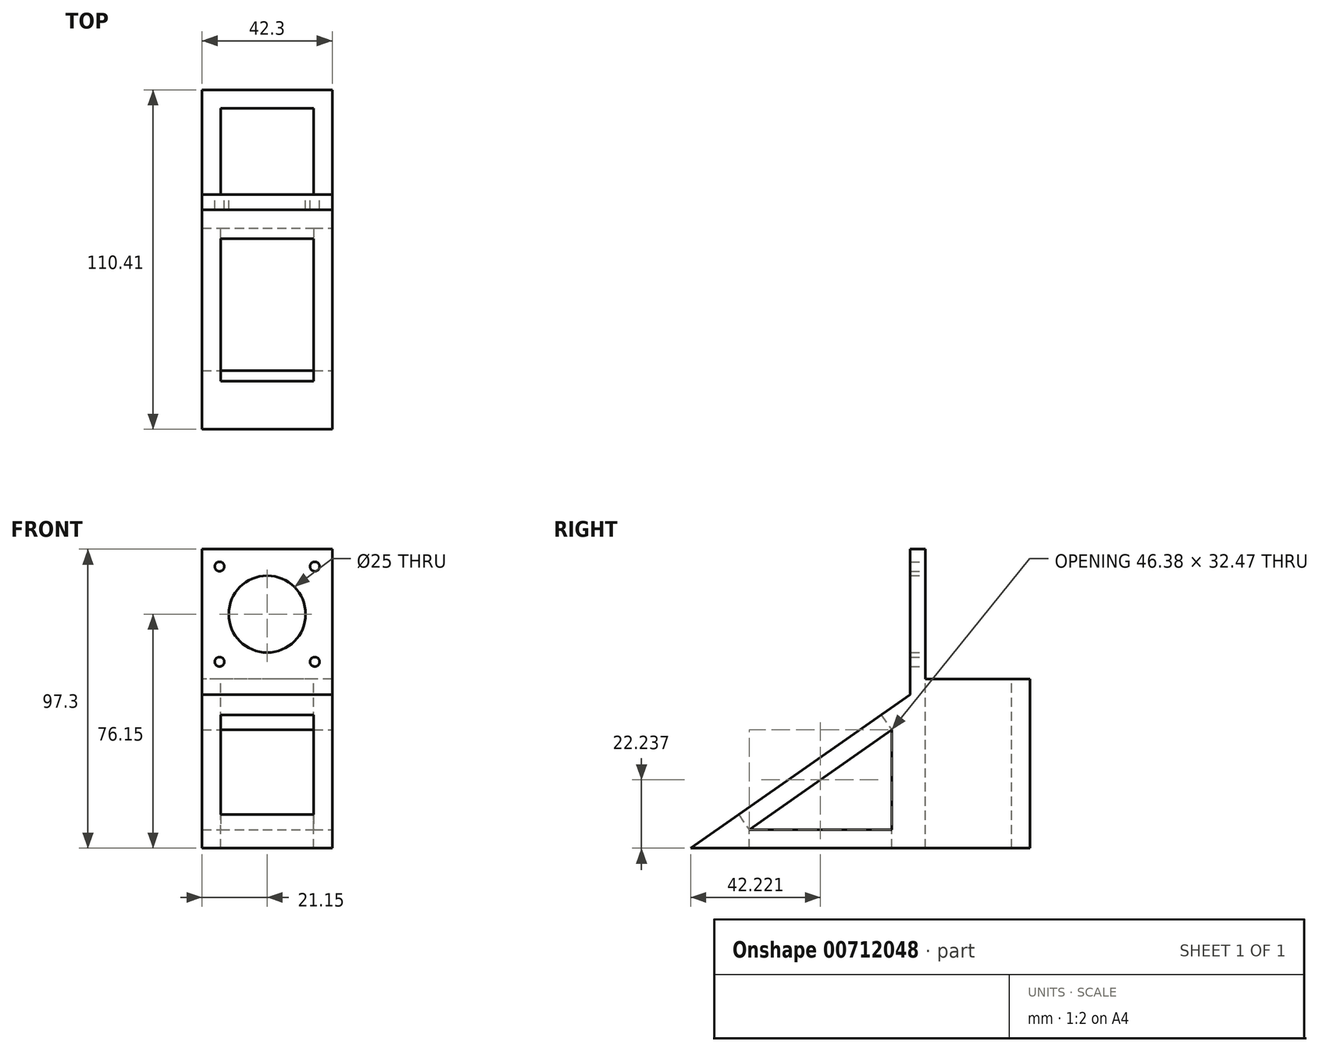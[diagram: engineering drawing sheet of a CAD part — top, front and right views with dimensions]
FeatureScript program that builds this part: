
annotation { "Feature Type Name" : "Feature", "Feature Type Description" : "" }
export const myFeature = defineFeature(function(context is Context, id is Id, definition is map)
    precondition{}
    {
        {
            var Q0;
            Q0=qCreatedBy(makeId("Front.planeOp"),FACE);
            var sketch = newSketch(context, id + "F0", { "sketchPlane" : qUnion([Q0])});
            skLineSegment(sketch, "E0.bottom", {"start": v(21.15, -21.15) * mm, "end": v(-21.15, -21.15) * mm});
            skLineSegment(sketch, "E0.top", {"start": v(21.15, 21.15) * mm, "end": v(-21.15, 21.15) * mm});
            skLineSegment(sketch, "E0.left", {"start": v(21.15, -21.15) * mm, "end": v(21.15, 21.15) * mm});
            skLineSegment(sketch, "E0.right", {"start": v(-21.15, -21.15) * mm, "end": v(-21.15, 21.15) * mm});
            skPoint(sketch, "E0.middle", {"position": v(0, 0) * mm});
            skPoint(sketch, "E1", {"position": v(15.5, 15.5) * mm});
            skPoint(sketch, "E2", {"position": v(-15.5, 15.5) * mm});
            skPoint(sketch, "E3", {"position": v(-15.5, -15.5) * mm});
            skPoint(sketch, "E4", {"position": v(15.5, -15.5) * mm});
            skCircle(sketch, "E5", {"center": v(0, 0) * mm, "radius": 12.5 * mm});
            skLineSegment(sketch, "E6", {"start": v(-21.15, -21.15) * mm, "end": v(-21.15, -26.15) * mm});
            skLineSegment(sketch, "E7", {"start": v(-21.15, -26.15) * mm, "end": v(21.15, -26.15) * mm});
            skLineSegment(sketch, "E8", {"start": v(21.15, -26.15) * mm, "end": v(21.15, -21.15) * mm});
            skSolve(sketch);
        }
        {
            var Q0;
            Q0=makeQuery(id+"F0.imprint","IMPRINT",FACE,{"disambiguationData":[TD([[makeQuery(id+"F0.imprint","IMPRINT",EDGE,{"derivedFrom":sQuery(id+"F0.wireOp",EDGE,"E0.bottom")}),-1.0]])]});
            var Q1;
            Q1=makeQuery(id+"F0.imprint","IMPRINT",FACE,{"disambiguationData":[TD([[makeQuery(id+"F0.imprint","IMPRINT",EDGE,{"derivedFrom":sQuery(id+"F0.wireOp",EDGE,"E0.top")}),1.0]])]});
            extrude(context, id + "F1", {"entities" : qUnion([Q0, Q1]), "depth" : 5 * mm, "offsetDistance" : 25 * mm});
        }
        {
            var Q0;
            Q0=sQuery(id+"F0.wireOp",VERTEX,"E2");
            var Q1;
            Q1=sQuery(id+"F0.wireOp",VERTEX,"E3");
            var Q2;
            Q2=sQuery(id+"F0.wireOp",VERTEX,"E4");
            var Q3;
            Q3=sQuery(id+"F0.wireOp",VERTEX,"E1");
            var Q4;
            Q4=makeQuery(id+"F1.opExtrude","SWEPT_BODY",BODY,{"disambiguationData":[OSD([sQuery(id+"F0.wireOp",EDGE,"E0.bottom"),sQuery(id+"F0.wireOp",EDGE,"E0.top"),sQuery(id+"F0.wireOp",EDGE,"E0.left"),sQuery(id+"F0.wireOp",EDGE,"E0.right")])]});
            hole(context, id + "F2", {"style" : HoleStyle.SIMPLE, "endStyle" : HoleEndStyle.THROUGH, "oppositeDirection" : true, "holeDiameter" : 3.1 * mm, "majorDiameter" : 5 * mm, "isTappedThrough" : true, "tappedDepth" : 12 * mm, "tapClearance" : 3, "locations" : qUnion([Q0, Q1, Q2, Q3]), "scope" : qUnion([Q4])});
        }
        {
            var Q0;
            Q0=makeQuery(id+"F0.imprint","IMPRINT",FACE,{"disambiguationData":[TD([[makeQuery(id+"F0.imprint","IMPRINT",EDGE,{"derivedFrom":sQuery(id+"F0.wireOp",EDGE,"E0.bottom")}),1.0]])]});
            extrude(context, id + "F3", {"entities" : qUnion([Q0]), "operationType" : NewBodyOperationType.ADD, "depth" : 5 * mm, "offsetDistance" : 25 * mm});
        }
        {
            var Q0;
            Q0=makeQuery(id+"F0.imprint","IMPRINT",FACE,{"disambiguationData":[TD([[makeQuery(id+"F0.imprint","IMPRINT",EDGE,{"derivedFrom":sQuery(id+"F0.wireOp",EDGE,"E0.bottom")}),1.0]])]});
            extrude(context, id + "F4", {"entities" : qUnion([Q0]), "operationType" : NewBodyOperationType.ADD, "oppositeDirection" : true, "depth" : 34 * mm, "offsetDistance" : 25 * mm});
        }
        {
            var Q0;
            Q0=makeQuery(id+"F4.opExtrude","SWEPT_FACE",FACE,{"disambiguationData":[OSD([sQuery(id+"F0.wireOp",EDGE,"E0.bottom")])]});
            var sketch = newSketch(context, id + "F5", { "sketchPlane" : qUnion([Q0])});
            skLineSegment(sketch, "E9", {"start": v(-15.15, 28) * mm, "end": v(-15.15, 0) * mm});
            skLineSegment(sketch, "E10", {"start": v(-15.15, 0) * mm, "end": v(15.15, 0) * mm});
            skLineSegment(sketch, "E11", {"start": v(15.15, 0) * mm, "end": v(15.15, 28) * mm});
            skLineSegment(sketch, "E12", {"start": v(15.15, 28) * mm, "end": v(-15.15, 28) * mm});
            skSolve(sketch);
        }
        {
            var Q0;
            Q0=makeQuery(id+"F5.imprint","IMPRINT",FACE,{"disambiguationData":[TD([[makeQuery(id+"F5.imprint","IMPRINT",EDGE,{"derivedFrom":sQuery(id+"F5.wireOp",EDGE,"E9")}),1.0]])]});
            extrude(context, id + "F6", {"entities" : qUnion([Q0]), "operationType" : NewBodyOperationType.REMOVE, "oppositeDirection" : true, "depth" : 5 * mm, "offsetDistance" : 25 * mm});
        }
        {
            var Q0;
            {var subQ0=sQuery(id+"F0.wireOp",EDGE,"E7");Q0=makeQuery(id+"F4.boolean.opBoolean","MERGE",FACE,{"derivedFrom":[makeQuery(id+"F3.opExtrude","SWEPT_FACE",FACE,{"disambiguationData":[OSD([subQ0])]}),makeQuery(id+"F4.opExtrude","SWEPT_FACE",FACE,{"disambiguationData":[OSD([subQ0])]})]});}
            extrude(context, id + "F7", {"entities" : qUnion([Q0]), "operationType" : NewBodyOperationType.ADD, "depth" : 50 * mm, "offsetDistance" : 25 * mm});
        }
        {
            var Q0;
            {var subQ0=sQuery(id+"F0.wireOp",EDGE,"E8");Q0=makeQuery(id+"F7.boolean.opBoolean","MERGE",FACE,{"derivedFrom":[makeQuery(id+"F4.boolean.opBoolean","MERGE",FACE,{"derivedFrom":[makeQuery(id+"F3.boolean.opBoolean","MERGE",FACE,{"derivedFrom":[makeQuery(id+"F1.opExtrude","SWEPT_FACE",FACE,{"disambiguationData":[OSD([sQuery(id+"F0.wireOp",EDGE,"E0.left")])]}),makeQuery(id+"F3.opExtrude","SWEPT_FACE",FACE,{"disambiguationData":[OSD([subQ0])]})]}),makeQuery(id+"F4.opExtrude","SWEPT_FACE",FACE,{"disambiguationData":[OSD([subQ0])]})]}),makeQuery(id+"F7.opExtrude","SWEPT_FACE",FACE,{"disambiguationData":[OSD([sQuery(id+"F0.wireOp",EDGE,"E7"),subQ0])]})]});}
            var sketch = newSketch(context, id + "F8", { "sketchPlane" : qUnion([Q0])});
            skLineSegment(sketch, "E13", {"start": v(-5, -76.15) * mm, "end": v(-76.4, -76.15) * mm});
            skLineSegment(sketch, "E14", {"start": v(-76.4, -76.15) * mm, "end": v(-5, -26.15) * mm});
            skLineSegment(sketch, "E15", {"start": v(-5, -26.15) * mm, "end": v(-5, -76.15) * mm});
            skLineSegment(sketch, "E16", {"start": v(-11, -37.68) * mm, "end": v(-11, -70.15) * mm});
            skLineSegment(sketch, "E17", {"start": v(-11, -70.15) * mm, "end": v(-57.38, -70.15) * mm});
            skLineSegment(sketch, "E18", {"start": v(-57.38, -70.15) * mm, "end": v(-11, -37.68) * mm});
            skSolve(sketch);
        }
        {
            var Q0;
            Q0=makeQuery(id+"F8.imprint","IMPRINT",FACE,{"disambiguationData":[TD([[makeQuery(id+"F8.imprint","IMPRINT",EDGE,{"derivedFrom":sQuery(id+"F8.wireOp",EDGE,"E13")}),-1.0]])]});
            extrude(context, id + "F9", {"entities" : qUnion([Q0]), "operationType" : NewBodyOperationType.ADD, "oppositeDirection" : true, "depth" : 42.3 * mm, "offsetDistance" : 25 * mm});
        }
        {
            var Q0;
            Q0=makeQuery(id+"F9.opExtrude","SWEPT_FACE",FACE,{"disambiguationData":[OSD([sQuery(id+"F8.wireOp",EDGE,"E18")])]});
            var sketch = newSketch(context, id + "F10", { "sketchPlane" : qUnion([Q0])});
            skLineSegment(sketch, "E19", {"start": v(15.15, 30.62) * mm, "end": v(-15.15, 30.62) * mm});
            skLineSegment(sketch, "E20", {"start": v(-15.15, 30.62) * mm, "end": v(-15.15, 87.24) * mm});
            skLineSegment(sketch, "E21", {"start": v(-15.15, 87.24) * mm, "end": v(15.15, 87.24) * mm});
            skLineSegment(sketch, "E22", {"start": v(15.15, 87.24) * mm, "end": v(15.15, 30.62) * mm});
            skSolve(sketch);
        }
        {
            var Q0;
            Q0=makeQuery(id+"F10.imprint","IMPRINT",FACE,{"disambiguationData":[TD([[makeQuery(id+"F10.imprint","IMPRINT",EDGE,{"derivedFrom":sQuery(id+"F10.wireOp",EDGE,"E19")}),1.0]])]});
            extrude(context, id + "F11", {"entities" : qUnion([Q0]), "operationType" : NewBodyOperationType.REMOVE, "oppositeDirection" : true, "depth" : 25 * mm, "offsetDistance" : 25 * mm});
        }
        {
            var Q0;
            Q0=makeQuery(id+"F9.opExtrude","SWEPT_FACE",FACE,{"disambiguationData":[OSD([sQuery(id+"F8.wireOp",EDGE,"E17")])]});
            var sketch = newSketch(context, id + "F12", { "sketchPlane" : qUnion([Q0])});
            skLineSegment(sketch, "E23", {"start": v(-15.15, -11) * mm, "end": v(15.15, -11) * mm});
            skLineSegment(sketch, "E24", {"start": v(15.15, -11) * mm, "end": v(15.15, -57.38) * mm});
            skLineSegment(sketch, "E25", {"start": v(15.15, -57.38) * mm, "end": v(-15.15, -57.38) * mm});
            skLineSegment(sketch, "E26", {"start": v(-15.15, -57.38) * mm, "end": v(-15.15, -11) * mm});
            skSolve(sketch);
        }
        {
            var Q0;
            Q0=makeQuery(id+"F12.imprint","IMPRINT",FACE,{"disambiguationData":[TD([[makeQuery(id+"F12.imprint","IMPRINT",EDGE,{"derivedFrom":sQuery(id+"F12.wireOp",EDGE,"E23")}),-1.0]])]});
            extrude(context, id + "F13", {"entities" : qUnion([Q0]), "operationType" : NewBodyOperationType.REMOVE, "oppositeDirection" : true, "depth" : 25 * mm, "offsetDistance" : 25 * mm});
        }
    });
